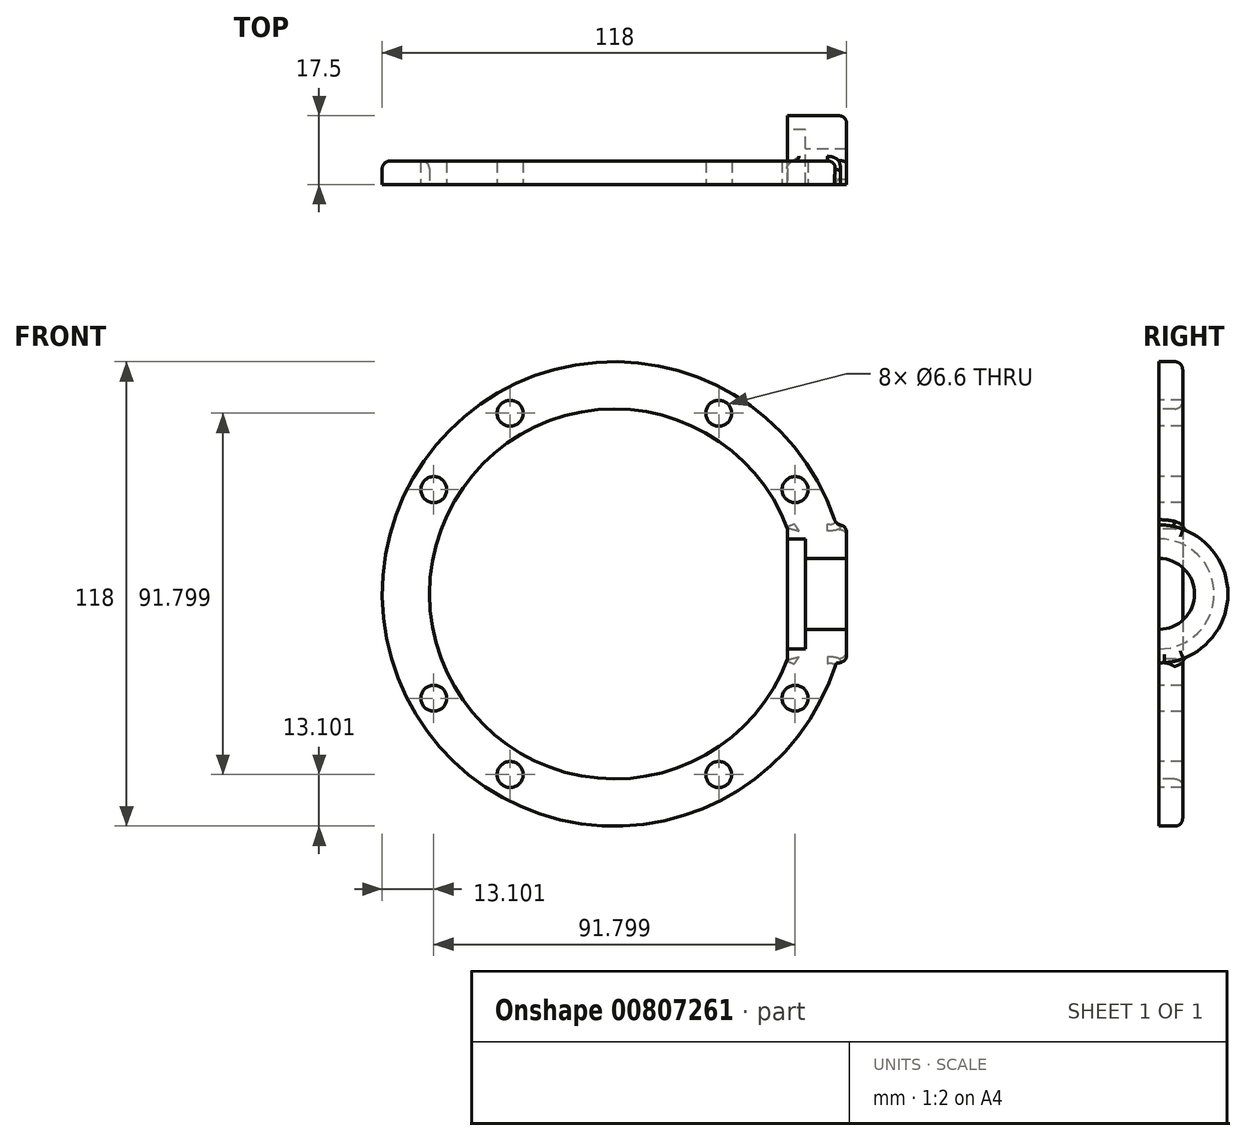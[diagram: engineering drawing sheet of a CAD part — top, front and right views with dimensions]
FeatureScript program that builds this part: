
annotation { "Feature Type Name" : "Feature", "Feature Type Description" : "" }
export const myFeature = defineFeature(function(context is Context, id is Id, definition is map)
    precondition{}
    {
        {
            var Q0;
            Q0=qCreatedBy(makeId("Front.planeOp"),FACE);
            var sketch = newSketch(context, id + "F0", { "sketchPlane" : qUnion([Q0])});
            skCircle(sketch, "E0", {"center": v(0, 0) * mm, "radius": 47 * mm});
            skCircle(sketch, "E1", {"center": v(0, 0) * mm, "radius": 59 * mm});
            skLineSegment(sketch, "E2", {"start": v(0, 0) * mm, "end": v(35.83, 0) * mm, "construction": true});
            skLineSegment(sketch, "E3", {"start": v(0, 0) * mm, "end": v(0, 36.97) * mm, "construction": true});
            skLineSegment(sketch, "E4", {"start": v(0, 0) * mm, "end": v(45.9, 26.5) * mm, "construction": true});
            skLineSegment(sketch, "E5.MirrorCS", {"start": v(0, 0) * mm, "end": v(45.9, -26.5) * mm, "construction": true});
            skCircle(sketch, "E6", {"center": v(45.9, 26.5) * mm, "radius": 3.3 * mm});
            skCircle(sketch, "E7", {"center": v(45.9, -26.5) * mm, "radius": 3.3 * mm});
            skCircle(sketch, "E8.1.0", {"center": v(-26.5, 45.9) * mm, "radius": 3.3 * mm});
            skCircle(sketch, "E8.1.1", {"center": v(26.5, 45.9) * mm, "radius": 3.3 * mm});
            skCircle(sketch, "E8.2.0", {"center": v(-45.9, -26.5) * mm, "radius": 3.3 * mm});
            skCircle(sketch, "E8.2.1", {"center": v(-45.9, 26.5) * mm, "radius": 3.3 * mm});
            skCircle(sketch, "E8.3.0", {"center": v(26.5, -45.9) * mm, "radius": 3.3 * mm});
            skCircle(sketch, "E8.3.1", {"center": v(-26.5, -45.9) * mm, "radius": 3.3 * mm});
            skCircle(sketch, "E9", {"center": v(0, 0) * mm, "radius": 53 * mm, "construction": true});
            skSolve(sketch);
        }
        {
            var Q0;
            Q0 = qSketchRegion(id + "F0", true);
            extrude(context, id + "F1", {"entities" : qUnion([Q0]), "oppositeDirection" : true, "depth" : 6 * mm, "offsetDistance" : 25 * mm});
        }
        {
            var Q0;
            Q0=qCreatedBy(makeId("Right.planeOp"),FACE);
            cPlane(context, id + "F2", {"entities" : qUnion([Q0]), "cplaneType" : CPlaneType.OFFSET, "offset" : (118 / 2) * mm, "width" : 150 * mm, "height" : 150 * mm});
        }
        {
            var Q0;
            Q0=qCreatedBy(id+"F2.planeOp",FACE);
            var sketch = newSketch(context, id + "F3", { "sketchPlane" : qUnion([Q0])});
            skLineSegment(sketch, "E10.0", {"start": v(0, -17.5) * mm, "end": v(0, 17.5) * mm});
            skArc(sketch, "E11", {"start": v(0, -17.5) * mm, "mid": v(17.5, 0) * mm, "end": v(0, 17.5) * mm});
            skPoint(sketch, "E12.orphan", {"position": v(6, 59) * mm});
            skPoint(sketch, "E13.orphan", {"position": v(0, 59) * mm});
            skPoint(sketch, "E14.orphan", {"position": v(0, -59) * mm});
            skPoint(sketch, "E15.orphan", {"position": v(6, -59) * mm});
            skSolve(sketch);
        }
        {
            var Q0;
            Q0 = qSketchRegion(id + "F3", true);
            extrude(context, id + "F4", {"entities" : qUnion([Q0]), "operationType" : NewBodyOperationType.ADD, "oppositeDirection" : true, "depth" : 15 * mm, "offsetDistance" : 25 * mm});
        }
        {
            var Q0;
            Q0=makeQuery(id+"F4.opExtrude","CAP_FACE",FACE,{"disambiguationData":[OSD([sQuery(id+"F3.wireOp",EDGE,"E10.0"),sQuery(id+"F3.wireOp",EDGE,"E11")])],"isStart":false});
            var sketch = newSketch(context, id + "F5", { "sketchPlane" : qUnion([Q0])});
            skPoint(sketch, "E16", {"position": v(0, 0) * mm});
            skSolve(sketch);
        }
        {
            var Q0;
            Q0=sQuery(id+"F5.wireOp",VERTEX,"E16");
            var Q1;
            Q1=makeQuery(id+"F1.opExtrude","SWEPT_BODY",BODY,{"disambiguationData":[OSD([sQuery(id+"F0.wireOp",EDGE,"E0"),sQuery(id+"F0.wireOp",EDGE,"E1"),sQuery(id+"F0.wireOp",EDGE,"E6"),sQuery(id+"F0.wireOp",EDGE,"E7"),sQuery(id+"F0.wireOp",EDGE,"E8.1.0"),sQuery(id+"F0.wireOp",EDGE,"E8.1.1"),sQuery(id+"F0.wireOp",EDGE,"E8.2.0"),sQuery(id+"F0.wireOp",EDGE,"E8.2.1"),sQuery(id+"F0.wireOp",EDGE,"E8.3.0"),sQuery(id+"F0.wireOp",EDGE,"E8.3.1")])]});
            hole(context, id + "F6", {"style" : HoleStyle.C_BORE, "endStyle" : HoleEndStyle.BLIND, "holeDiameter" : 18 * mm, "cBoreDiameter" : 28 * mm, "cBoreDepth" : ((97 - 88) / 2) * mm, "majorDiameter" : 5 * mm, "holeDepth" : 15 * mm, "tappedDepth" : 12 * mm, "tapClearance" : 3, "startFromSketch" : true, "locations" : qUnion([Q0]), "scope" : qUnion([Q1])});
        }
        {
            var Q0;
            Q0=makeQuery(id+"F4.boolean.opBoolean","INTERSECT",EDGE,{"disambiguationData":[OD(1.0)],"derivedFrom":[makeQuery(id+"F1.opExtrude","CAP_FACE",FACE,{"disambiguationData":[OSD([sQuery(id+"F0.wireOp",EDGE,"E0"),sQuery(id+"F0.wireOp",EDGE,"E1"),sQuery(id+"F0.wireOp",EDGE,"E6"),sQuery(id+"F0.wireOp",EDGE,"E7"),sQuery(id+"F0.wireOp",EDGE,"E8.1.0"),sQuery(id+"F0.wireOp",EDGE,"E8.1.1"),sQuery(id+"F0.wireOp",EDGE,"E8.2.0"),sQuery(id+"F0.wireOp",EDGE,"E8.2.1"),sQuery(id+"F0.wireOp",EDGE,"E8.3.0"),sQuery(id+"F0.wireOp",EDGE,"E8.3.1")])],"isStart":false}),makeQuery(id+"F4.opExtrude","SWEPT_FACE",FACE,{"disambiguationData":[OSD([sQuery(id+"F3.wireOp",EDGE,"E11")])]})]});
            var Q1;
            Q1=makeQuery(id+"F4.boolean.opBoolean","INTERSECT",EDGE,{"disambiguationData":[OD(1.0)],"derivedFrom":[makeQuery(id+"F1.opExtrude","SWEPT_FACE",FACE,{"disambiguationData":[OSD([sQuery(id+"F0.wireOp",EDGE,"E1")])]}),makeQuery(id+"F4.opExtrude","SWEPT_FACE",FACE,{"disambiguationData":[OSD([sQuery(id+"F3.wireOp",EDGE,"E11")])]})]});
            var Q2;
            Q2=makeQuery(id+"F1.opExtrude","CAP_EDGE",EDGE,{"disambiguationData":[OSD([sQuery(id+"F0.wireOp",EDGE,"E1")])],"isStart":false});
            var Q3;
            Q3=makeQuery(id+"F4.boolean.opBoolean","INTERSECT",EDGE,{"disambiguationData":[OD(0.0)],"derivedFrom":[makeQuery(id+"F1.opExtrude","CAP_FACE",FACE,{"disambiguationData":[OSD([sQuery(id+"F0.wireOp",EDGE,"E0"),sQuery(id+"F0.wireOp",EDGE,"E1"),sQuery(id+"F0.wireOp",EDGE,"E6"),sQuery(id+"F0.wireOp",EDGE,"E7"),sQuery(id+"F0.wireOp",EDGE,"E8.1.0"),sQuery(id+"F0.wireOp",EDGE,"E8.1.1"),sQuery(id+"F0.wireOp",EDGE,"E8.2.0"),sQuery(id+"F0.wireOp",EDGE,"E8.2.1"),sQuery(id+"F0.wireOp",EDGE,"E8.3.0"),sQuery(id+"F0.wireOp",EDGE,"E8.3.1")])],"isStart":false}),makeQuery(id+"F4.opExtrude","SWEPT_FACE",FACE,{"disambiguationData":[OSD([sQuery(id+"F3.wireOp",EDGE,"E11")])]})]});
            fillet(context, id + "F7", {"entities" : qUnion([Q0, Q1, Q2, Q3]), "radius" : 2 * mm, "tangentPropagation" : true, "allowEdgeOverflow" : false});
        }
        {
            var Q0;
            Q0=makeQuery(id+"F4.opExtrude","CAP_EDGE",EDGE,{"disambiguationData":[OSD([sQuery(id+"F3.wireOp",EDGE,"E11")])],"isStart":true});
            var Q1;
            Q1=makeQuery(id+"F1.opExtrude","CAP_EDGE",EDGE,{"disambiguationData":[OSD([sQuery(id+"F0.wireOp",EDGE,"E0")])],"isStart":false});
            fillet(context, id + "F8", {"entities" : qUnion([Q0, Q1]), "radius" : 2 * mm, "tangentPropagation" : true, "allowEdgeOverflow" : false});
        }
    });
